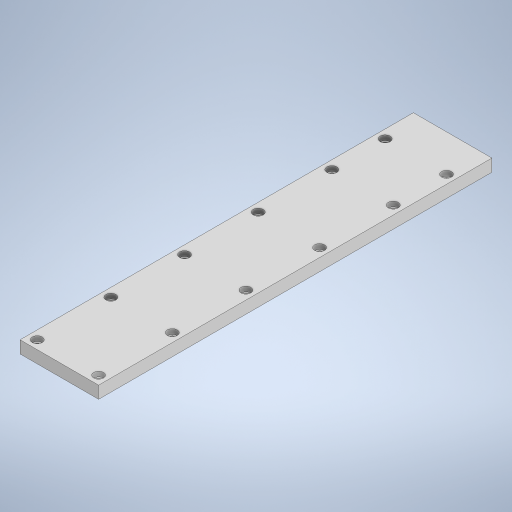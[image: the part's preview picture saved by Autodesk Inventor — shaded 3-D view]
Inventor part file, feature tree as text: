
AUTODESK INVENTOR PART (.ipt)
format: ipt  version: 2023 (Build 270158000, 158)  size: 360,960 bytes
history: native  units: mm
features: sketch x4, extrude x2, hole x2, fillet x1
ambient origin geometry x8: Origin, YZ Plane, XZ Plane, XY Plane, X Axis, Y Axis, Z Axis, Center Point
bodies: Solid1 (feature_tree)
feature tree (9):
  extrude  "Extrusion1"  Depth=32.0mm
  hole  "Hole1"  [1 undecoded]
  hole  "Hole2"  [1 undecoded]
  extrude  "Extrusion2"  Depth=0.5mm
  fillet  "Fillet2"  Radius=0.5mm
  sketch  "Sketch1"  dims[d0=160.2mm d1=32.0mm]
  sketch  "Sketch2"  dims[d2=5.0mm d3=0.0mm d4=3.5mm]
  sketch  "Sketch3"  dims[d5=3.5mm d6=50.0mm d8=30.0mm d9=10.0mm d11=10.0mm]
  sketch  "Sketch6"  dims[d13=15.0mm d14=2.38125mm d15=6.0mm d16=4.0mm d17=2.0mm d18=90.0deg d19=10.0mm d20=20.594885mm d22=3.0mm d23=2.38125mm d24=6.0mm d25=4.0mm d26=2.0mm d27=90.0deg d28=10.0mm d29=20.594885mm d36=0.5mm d37=0.0mm d38=1.5mm d40=0.5mm]
note: 2 required parameter values undecoded (feature->parameter linkage not recoverable at this tier; creation-order binding heuristic only, values carry confidence <= 0.55)
